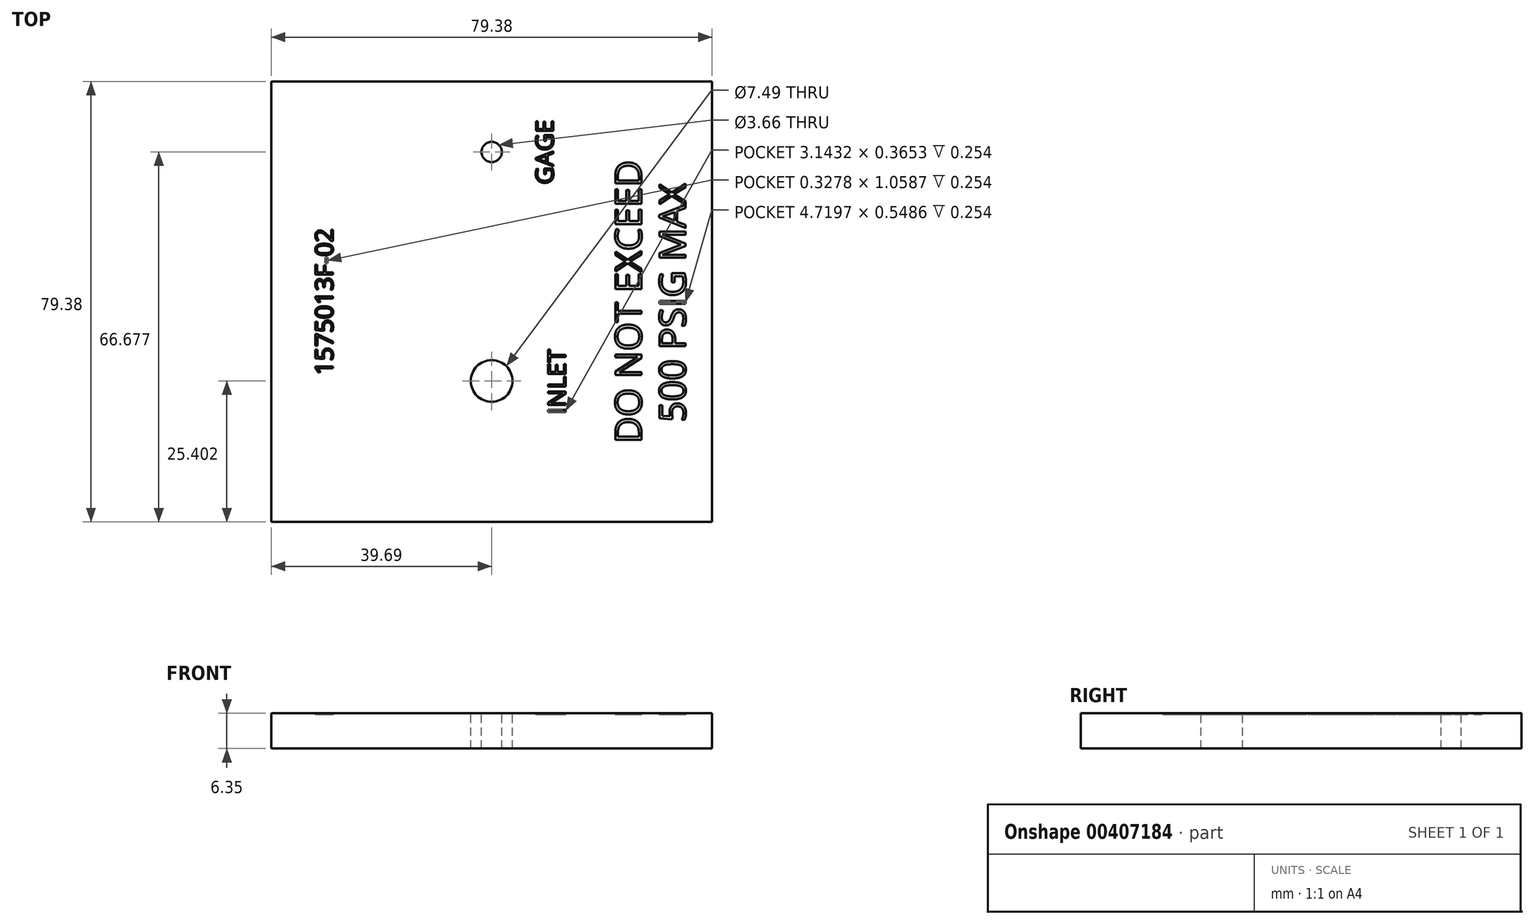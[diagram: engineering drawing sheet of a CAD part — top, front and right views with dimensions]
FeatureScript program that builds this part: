
annotation { "Feature Type Name" : "Feature", "Feature Type Description" : "" }
export const myFeature = defineFeature(function(context is Context, id is Id, definition is map)
    precondition{}
    {
        {
            var Q0;
            Q0=qCreatedBy(makeId("Top.planeOp"),FACE);
            var sketch = newSketch(context, id + "F0", { "sketchPlane" : qUnion([Q0])});
            skLineSegment(sketch, "E0.bottom", {"start": v(39.69, 39.69) * mm, "end": v(-39.69, 39.69) * mm});
            skLineSegment(sketch, "E0.top", {"start": v(39.69, -39.69) * mm, "end": v(-39.69, -39.69) * mm});
            skLineSegment(sketch, "E0.left", {"start": v(39.69, 39.69) * mm, "end": v(39.69, -39.69) * mm});
            skLineSegment(sketch, "E0.right", {"start": v(-39.69, 39.69) * mm, "end": v(-39.69, -39.69) * mm});
            skPoint(sketch, "E0.middle", {"position": v(0, 0) * mm});
            skSolve(sketch);
        }
        {
            var Q0;
            Q0=qSketchRegion(id+"F0",true);
            extrude(context, id + "F1", {"entities" : qUnion([Q0]), "depth" : 6.35 * mm});
        }
        {
            var Q0;
            Q0=makeQuery(id+"F1.opExtrude","CAP_FACE",FACE,{"disambiguationData":[OSD([sQuery(id+"F0.wireOp",EDGE,"E0.bottom"),sQuery(id+"F0.wireOp",EDGE,"E0.top"),sQuery(id+"F0.wireOp",EDGE,"E0.left"),sQuery(id+"F0.wireOp",EDGE,"E0.right")])],"isStart":false});
            var sketch = newSketch(context, id + "F2", { "sketchPlane" : qUnion([Q0])});
            skLineSegment(sketch, "E1", {"start": v(0, 39.69) * mm, "end": v(0, -39.69) * mm, "construction": true});
            skCircle(sketch, "E2", {"center": v(0, 26.99) * mm, "radius": 1.83 * mm});
            skCircle(sketch, "E3", {"center": v(0, -14.29) * mm, "radius": 3.75 * mm});
            skText(sketch, "E4", { "text": "INLET", "fontName": "OpenSans-Regular.ttf"});
            skPoint(sketch, "E5", {"position": v(11.75, -14.29) * mm});
            skText(sketch, "E6", { "text": "GAGE", "fontName": "OpenSans-Regular.ttf"});
            skPoint(sketch, "E7", {"position": v(9.53, 26.99) * mm});
            skText(sketch, "E8", { "text": "DO NOT EXCEED", "fontName": "OpenSans-Regular.ttf"});
            skText(sketch, "E9", { "text": "500 PSIG MAX", "fontName": "OpenSans-Regular.ttf"});
            skPoint(sketch, "E10", {"position": v(24.6, 0) * mm});
            skPoint(sketch, "E11", {"position": v(32.54, 0) * mm});
            skText(sketch, "E12", { "text": "1575013F-02", "fontName": "OpenSans-Regular.ttf"});
            skPoint(sketch, "E13", {"position": v(-30.16, 0) * mm});
            const initialGuessF2  = {"E4": [0.01333, -0.02028, 0, 1, 0.00317], "E6": [0.01111, 0.02115, 0, 1, 0.00317], "E8": [0.02699, -0.02554, 0, 1, 0.00476], "E9": [0.03493, -0.02172, 0, 1, 0.00476], "E12": [-0.02858, -0.01322, 0, 1, 0.00318]};
            skSetInitialGuess(sketch, initialGuessF2);
            skSolve(sketch);
        }
        {
            var Q0;
            Q0=makeQuery(id+"F2.imprint","IMPRINT",FACE,{"disambiguationData":[TD([[makeQuery(id+"F2.imprint","IMPRINT",EDGE,{"derivedFrom":sQuery(id+"F2.wireOp",EDGE,"E2")}),1.0]])]});
            var Q1;
            Q1=makeQuery(id+"F2.imprint","IMPRINT",FACE,{"disambiguationData":[TD([[makeQuery(id+"F2.imprint","IMPRINT",EDGE,{"derivedFrom":sQuery(id+"F2.wireOp",EDGE,"E3")}),1.0]])]});
            extrude(context, id + "F3", {"entities" : qUnion([Q0, Q1]), "operationType" : NewBodyOperationType.REMOVE, "oppositeDirection" : true, "depth" : 25.4 * mm});
        }
        {
            var Q0;
            Q0 = qSketchRegion(id + "F2", true);
            extrude(context, id + "F4", {"entities" : qUnion([Q0]), "operationType" : NewBodyOperationType.REMOVE, "oppositeDirection" : true, "depth" : 0.25 * mm});
        }
    });
